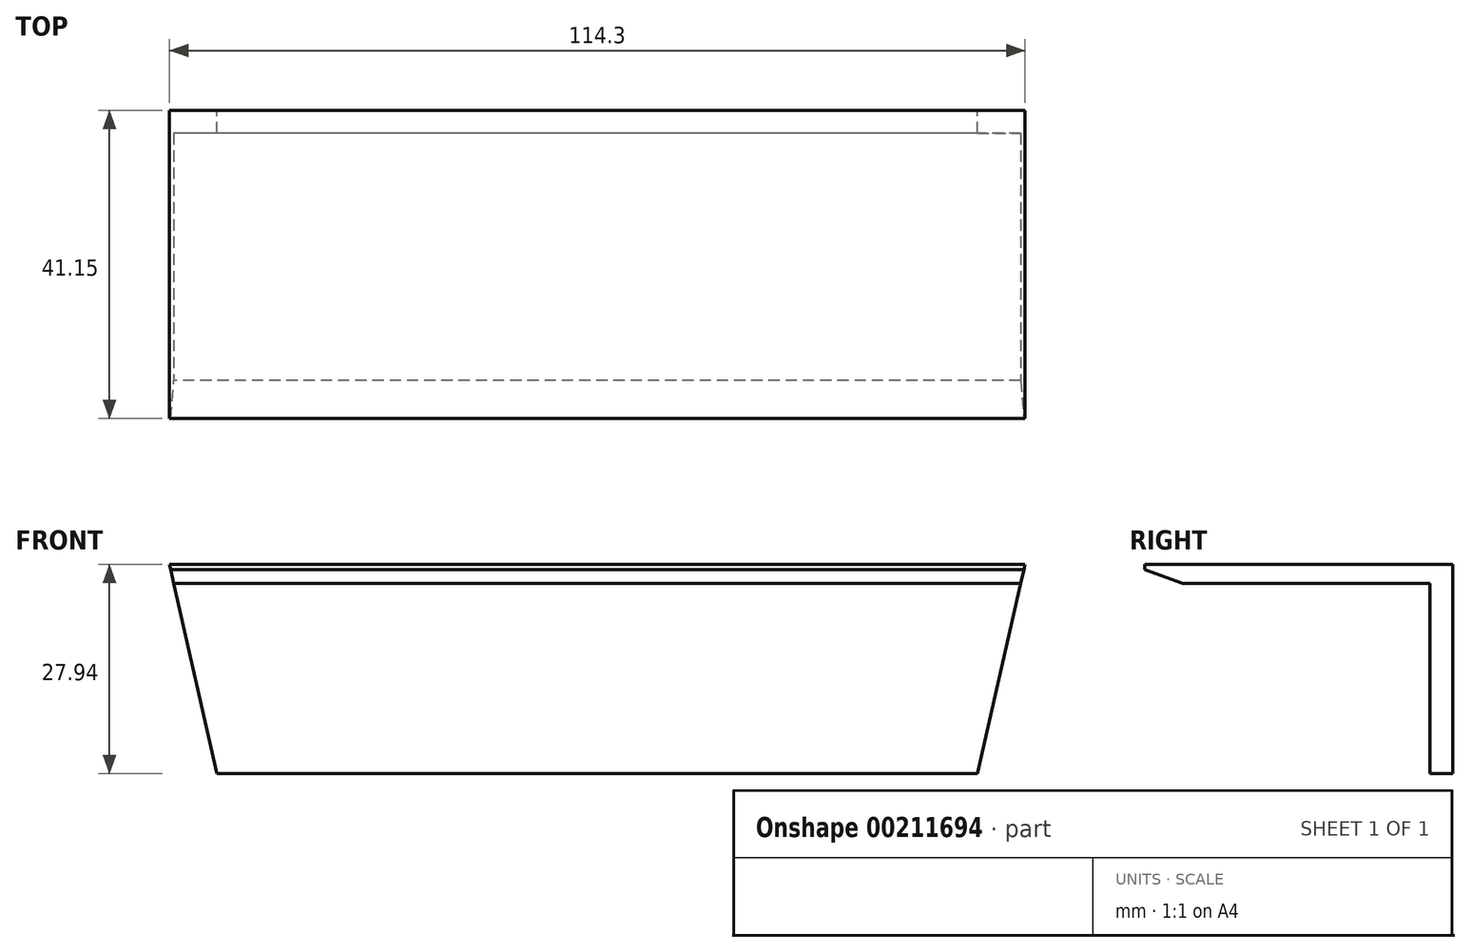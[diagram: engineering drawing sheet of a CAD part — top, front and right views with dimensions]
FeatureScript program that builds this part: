
annotation { "Feature Type Name" : "Feature", "Feature Type Description" : "" }
export const myFeature = defineFeature(function(context is Context, id is Id, definition is map)
    precondition{}
    {
        {
            var Q0;
            Q0=qCreatedBy(makeId("Right.planeOp"),FACE);
            var sketch = newSketch(context, id + "F0", { "sketchPlane" : qUnion([Q0])});
            skLineSegment(sketch, "E0", {"start": v(0, 0) * mm, "end": v(0, 25.4) * mm});
            skLineSegment(sketch, "E1", {"start": v(0, 25.4) * mm, "end": v(-38.1, 25.4) * mm});
            skLineSegment(sketch, "E2", {"start": v(-38.1, 25.4) * mm, "end": v(-38.1, 27.94) * mm});
            skLineSegment(sketch, "E3", {"start": v(-38.1, 27.94) * mm, "end": v(3.05, 27.94) * mm});
            skLineSegment(sketch, "E4", {"start": v(3.05, 27.94) * mm, "end": v(3.05, 0) * mm});
            skLineSegment(sketch, "E5", {"start": v(3.05, 0) * mm, "end": v(0, 0) * mm});
            skSolve(sketch);
        }
        {
            var Q0;
            Q0=makeQuery(id+"F0.imprint","IMPRINT",FACE,{"disambiguationData":[TD([[makeQuery(id+"F0.imprint","IMPRINT",EDGE,{"derivedFrom":sQuery(id+"F0.wireOp",EDGE,"E0")}),-1.0]])]});
            extrude(context, id + "F1", {"entities" : qUnion([Q0]), "depth" : 114.3 * mm});
        }
        {
            var Q0;
            Q0=makeQuery(id+"F1.opExtrude","SWEPT_FACE",FACE,{"disambiguationData":[OSD([sQuery(id+"F0.wireOp",EDGE,"E4")])]});
            var sketch = newSketch(context, id + "F2", { "sketchPlane" : qUnion([Q0])});
            skLineSegment(sketch, "E6", {"start": v(-114.3, 27.94) * mm, "end": v(-107.95, 0) * mm});
            skLineSegment(sketch, "E7", {"start": v(0, 27.94) * mm, "end": v(-6.35, 0) * mm});
            skLineSegment(sketch, "E8", {"start": v(-114.3, 0) * mm, "end": v(-107.95, 0) * mm});
            skLineSegment(sketch, "E9", {"start": v(-6.35, 0) * mm, "end": v(0, 0) * mm});
            skSolve(sketch);
        }
        {
            var Q0;
            Q0=makeQuery(id+"F2.imprint","IMPRINT",FACE,{"disambiguationData":[TD([[makeQuery(id+"F2.imprint","IMPRINT",EDGE,{"derivedFrom":sQuery(id+"F2.wireOp",EDGE,"E6")}),-1.0]])]});
            var Q1;
            Q1=makeQuery(id+"F2.imprint","IMPRINT",FACE,{"disambiguationData":[TD([[makeQuery(id+"F2.imprint","IMPRINT",EDGE,{"derivedFrom":sQuery(id+"F2.wireOp",EDGE,"E7")}),1.0]])]});
            extrude(context, id + "F3", {"entities" : qUnion([Q0, Q1]), "operationType" : NewBodyOperationType.REMOVE, "endBound" : BoundingType.THROUGH_ALL, "oppositeDirection" : true, "depth" : 25.4 * mm});
        }
        {
            var Q0;
            Q0=makeQuery(id+"F1.opExtrude","SWEPT_EDGE",EDGE,{"disambiguationData":[OSD([sQuery(id+"F0.wireOp",EDGE,"E1"),sQuery(id+"F0.wireOp",EDGE,"E2")])]});
            chamfer(context, id + "F4", {"entities" : qUnion([Q0]), "chamferType" : ChamferType.OFFSET_ANGLE, "width" : 5.08 * mm, "oppositeDirection" : false, "angle" : 20 * degree, "tangentPropagation" : true});
        }
    });
